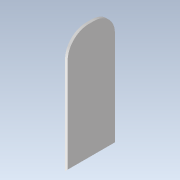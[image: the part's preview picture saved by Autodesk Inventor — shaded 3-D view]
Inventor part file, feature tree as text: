
AUTODESK INVENTOR PART (.ipt)
format: ipt  version: 2021 (Build 250183000, 183)  size: 89,600 bytes
history: native  units: mm
features: sketch x2, other x1, extrude x1, chamfer x1, fillet x1, hole x1
ambient origin geometry x8: Origin, YZ Plane, XZ Plane, XY Plane, X Axis, Y Axis, Z Axis, Center Point
bodies: Body1 (feature_tree)
feature tree (7):
  other  "Sólido1"
  extrude  "Extrusión1"  Depth=45.0mm
  chamfer  "Chaflán1"  Distance=1.0mm Angle=45.0deg
  fillet  "Empalme1"  Radius=8.0mm
  hole  "Agujero1"  [1 undecoded]
  sketch  "Boceto1"  dims[d0=1.0mm d1=0.0mm d2=45.0mm]
  sketch  "Boceto2"  dims[d3=18.0mm d4=1.0mm d5=2.0mm d6=45.0deg d7=8.0mm d8=3.4mm d9=6.0mm d10=4.0mm d11=2.0mm d12=90.0deg d13=8.0mm d14=0.0mm]
note: 1 required parameter value undecoded (feature->parameter linkage not recoverable at this tier; creation-order binding heuristic only, values carry confidence <= 0.55)
